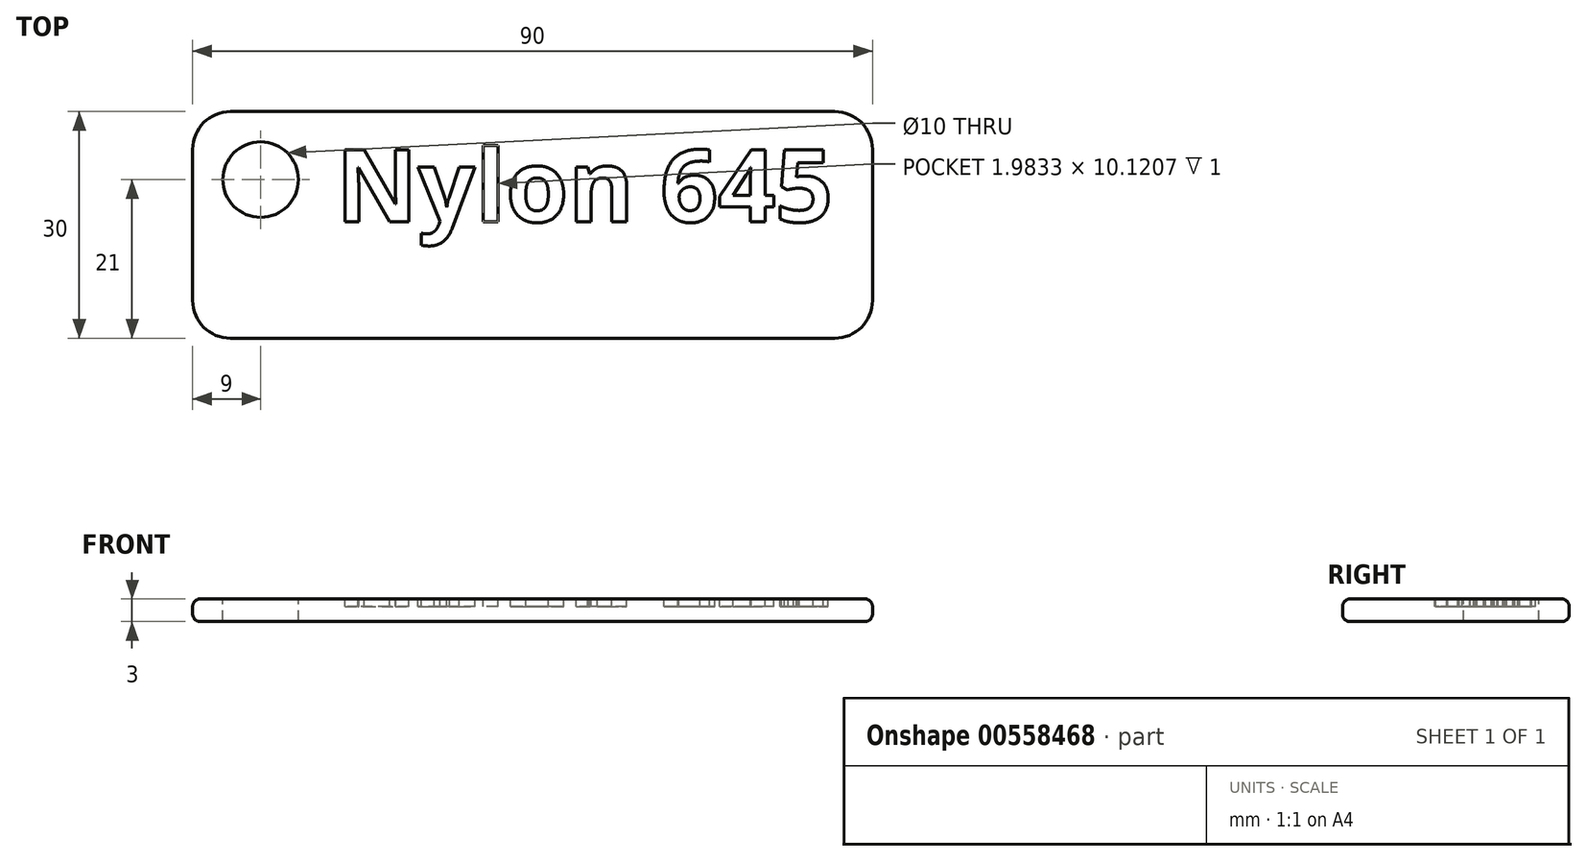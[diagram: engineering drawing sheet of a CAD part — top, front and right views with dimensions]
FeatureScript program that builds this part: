
annotation { "Feature Type Name" : "Feature", "Feature Type Description" : "" }
export const myFeature = defineFeature(function(context is Context, id is Id, definition is map)
    precondition{}
    {
        {
            var Q0;
            Q0=qCreatedBy(makeId("Top.planeOp"),FACE);
            var sketch = newSketch(context, id + "F0", { "sketchPlane" : qUnion([Q0])});
            skLineSegment(sketch, "E0.bottom", {"start": v(-45, 15) * mm, "end": v(45, 15) * mm});
            skLineSegment(sketch, "E0.top", {"start": v(-45, -15) * mm, "end": v(45, -15) * mm});
            skLineSegment(sketch, "E0.left", {"start": v(-45, 15) * mm, "end": v(-45, -15) * mm});
            skLineSegment(sketch, "E0.right", {"start": v(45, 15) * mm, "end": v(45, -15) * mm});
            skLineSegment(sketch, "E1", {"start": v(-45, 15) * mm, "end": v(45, -15) * mm, "construction": true});
            skSolve(sketch);
        }
        {
            var Q0;
            Q0=makeQuery(id+"F0.imprint","IMPRINT",FACE,{"disambiguationData":[TD([[makeQuery(id+"F0.imprint","IMPRINT",EDGE,{"derivedFrom":sQuery(id+"F0.wireOp",EDGE,"E0.bottom")}),-1.0]])]});
            extrude(context, id + "F1", {"entities" : qUnion([Q0]), "depth" : 3 * mm});
        }
        {
            var Q0;
            Q0=makeQuery(id+"F1.opExtrude","CAP_FACE",FACE,{"disambiguationData":[OSD([sQuery(id+"F0.wireOp",EDGE,"E0.bottom"),sQuery(id+"F0.wireOp",EDGE,"E0.top"),sQuery(id+"F0.wireOp",EDGE,"E0.left"),sQuery(id+"F0.wireOp",EDGE,"E0.right")])],"isStart":false});
            var Q1;
            Q1=makeQuery(id+"F1.opExtrude","CAP_FACE",FACE,{"disambiguationData":[OSD([sQuery(id+"F0.wireOp",EDGE,"E0.bottom"),sQuery(id+"F0.wireOp",EDGE,"E0.top"),sQuery(id+"F0.wireOp",EDGE,"E0.left"),sQuery(id+"F0.wireOp",EDGE,"E0.right")])],"isStart":true});
            fillet(context, id + "F2", {"entities" : qUnion([Q0, Q1]), "radius" : 1 * mm, "tangentPropagation" : true, "allowEdgeOverflow" : false});
        }
        {
            var Q0;
            Q0=makeQuery(id+"F1.opExtrude","SWEPT_EDGE",EDGE,{"disambiguationData":[OSD([sQuery(id+"F0.wireOp",EDGE,"E0.top"),sQuery(id+"F0.wireOp",EDGE,"E0.right")])]});
            var Q1;
            Q1=makeQuery(id+"F1.opExtrude","SWEPT_EDGE",EDGE,{"disambiguationData":[OSD([sQuery(id+"F0.wireOp",EDGE,"E0.bottom"),sQuery(id+"F0.wireOp",EDGE,"E0.right")])]});
            var Q2;
            Q2=makeQuery(id+"F1.opExtrude","SWEPT_EDGE",EDGE,{"disambiguationData":[OSD([sQuery(id+"F0.wireOp",EDGE,"E0.bottom"),sQuery(id+"F0.wireOp",EDGE,"E0.left")])]});
            var Q3;
            Q3=makeQuery(id+"F1.opExtrude","SWEPT_EDGE",EDGE,{"disambiguationData":[OSD([sQuery(id+"F0.wireOp",EDGE,"E0.top"),sQuery(id+"F0.wireOp",EDGE,"E0.left")])]});
            fillet(context, id + "F3", {"entities" : qUnion([Q0, Q1, Q2, Q3]), "radius" : 5 * mm, "tangentPropagation" : true, "allowEdgeOverflow" : false});
        }
        {
            var Q0;
            {var subQ0=sQuery(id+"F0.wireOp",EDGE,"E0.left");var subQ2=sQuery(id+"F0.wireOp",EDGE,"E0.bottom");var subQ4=sQuery(id+"F0.wireOp",EDGE,"E0.right");var subQ6=sQuery(id+"F0.wireOp",EDGE,"E0.top");Q0=makeQuery(id+"FmQCBBX3Ub0qneL_1.boolean.opBoolean","SPLIT",FACE,{"disambiguationData":[TD([makeQuery(id+"FmQCBBX3Ub0qneL_1.opExtrude","SWEPT_FACE",FACE,{"disambiguationData":[OSD([sQuery(id+"FOCoeRmDbjhRCuz_1.wireOp",EDGE,"4a1fb44a-e7be-4e23-9449-000d953c446c.sketch_text.stroke-0")])]})])],"derivedFrom":makeQuery(id+"F1.opExtrude","CAP_FACE",FACE,{"disambiguationData":[OSD([subQ2,subQ6,subQ0,subQ4])],"isStart":false})});}
            var sketch = newSketch(context, id + "F4", { "sketchPlane" : qUnion([Q0])});
            skCircle(sketch, "E2", {"center": v(-36, 6) * mm, "radius": 5 * mm});
            skSolve(sketch);
        }
        {
            var Q0;
            Q0=qSketchRegion(id+"F4",true);
            extrude(context, id + "F5", {"entities" : qUnion([Q0]), "operationType" : NewBodyOperationType.REMOVE, "oppositeDirection" : true, "depth" : 3 * mm});
        }
        {
            var Q0;
            Q0=makeQuery(id+"F1.opExtrude","CAP_FACE",FACE,{"disambiguationData":[OSD([sQuery(id+"F0.wireOp",EDGE,"E0.bottom"),sQuery(id+"F0.wireOp",EDGE,"E0.top"),sQuery(id+"F0.wireOp",EDGE,"E0.left"),sQuery(id+"F0.wireOp",EDGE,"E0.right")])],"isStart":false});
            var sketch = newSketch(context, id + "F6", { "sketchPlane" : qUnion([Q0])});
            skText(sketch, "E3", { "text": "Nylon 645", "fontName": "OpenSans-Bold.ttf"});
            const initialGuessF6  = {"E3": [-0.026, 0.00041, 1, 0, 0.00959]};
            skSetInitialGuess(sketch, initialGuessF6);
            skSolve(sketch);
        }
        {
            var Q0;
            Q0=qSketchRegion(id+"F6",true);
            extrude(context, id + "F7", {"entities" : qUnion([Q0]), "operationType" : NewBodyOperationType.REMOVE, "oppositeDirection" : true, "depth" : 1 * mm});
        }
    });
